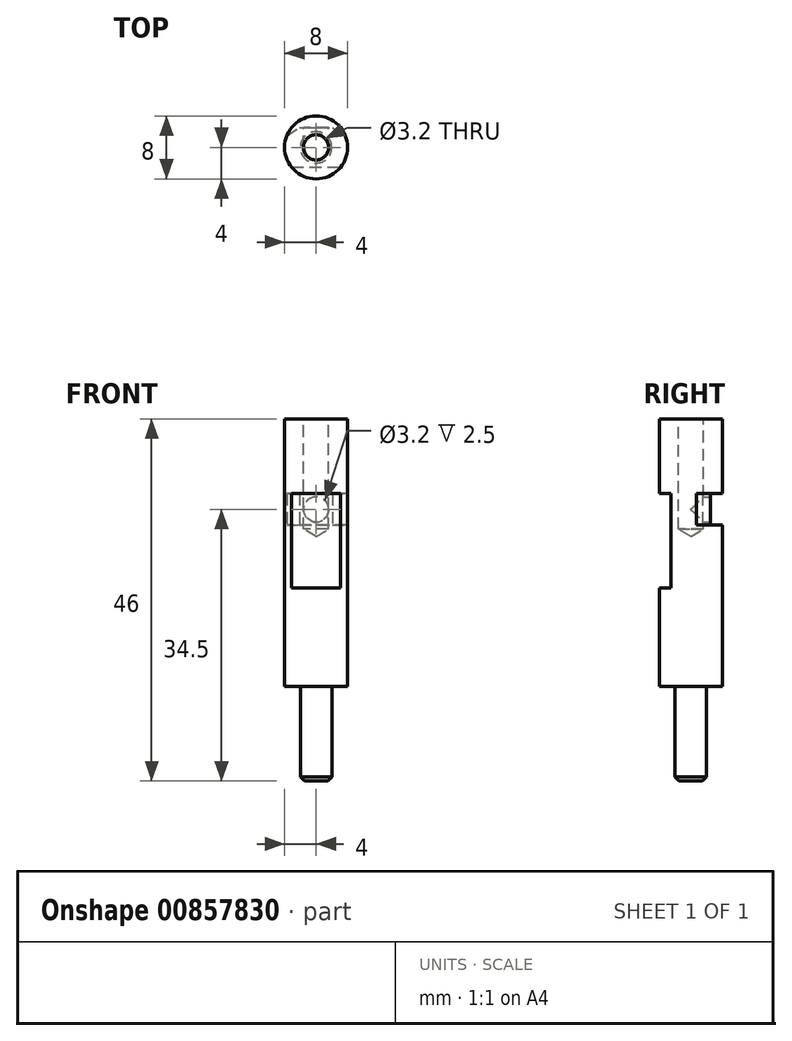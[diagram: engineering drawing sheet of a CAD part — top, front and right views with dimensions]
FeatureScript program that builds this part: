
annotation { "Feature Type Name" : "Feature", "Feature Type Description" : "" }
export const myFeature = defineFeature(function(context is Context, id is Id, definition is map)
    precondition{}
    {
        {
            var Q0;
            Q0=qCreatedBy(makeId("Front.planeOp"),FACE);
            var sketch = newSketch(context, id + "F0", { "sketchPlane" : qUnion([Q0])});
            skLineSegment(sketch, "E0", {"start": v(0, 0) * mm, "end": v(-2, 0) * mm});
            skLineSegment(sketch, "E1", {"start": v(-2, 0) * mm, "end": v(-2, 12) * mm});
            skLineSegment(sketch, "E2", {"start": v(-2, 12) * mm, "end": v(-4, 12) * mm});
            skLineSegment(sketch, "E3", {"start": v(-4, 12) * mm, "end": v(-4, 24.5) * mm});
            skLineSegment(sketch, "E4", {"start": v(-4, 24.5) * mm, "end": v(0, 24.5) * mm});
            skLineSegment(sketch, "E5", {"start": v(0, 24.5) * mm, "end": v(0, 0) * mm});
            skSolve(sketch);
        }
        {
            var Q0;
            Q0=makeQuery(id+"F0.imprint","IMPRINT",FACE,{"disambiguationData":[TD([[makeQuery(id+"F0.imprint","IMPRINT",EDGE,{"derivedFrom":sQuery(id+"F0.wireOp",EDGE,"E0")}),-1.0]])]});
            var Q1;
            Q1=sQuery(id+"F0.wireOp",EDGE,"E5");
            revolve(context, id + "F1", {"surfaceOperationType" : NewSurfaceOperationType.NEW, "entities" : qUnion([Q0]), "axis" : qUnion([Q1]), "revolveType" : RevolveType.FULL});
        }
        {
            var Q0;
            Q0=makeQuery(id+"F1.opRevolve","SWEPT_EDGE",EDGE,{"disambiguationData":[OSD([sQuery(id+"F0.wireOp",EDGE,"E0"),sQuery(id+"F0.wireOp",EDGE,"E1")])]});
            chamfer(context, id + "F2", {"entities" : qUnion([Q0]), "width" : 0.5 * mm, "tangentPropagation" : true});
        }
        {
            var Q0;
            Q0=makeQuery(id+"F1.opRevolve","SWEPT_FACE",FACE,{"disambiguationData":[OSD([sQuery(id+"F0.wireOp",EDGE,"E4")])]});
            var sketch = newSketch(context, id + "F3", { "sketchPlane" : qUnion([Q0])});
            skArc(sketch, "E6.0.0", {"start": v(3.12, -2.5) * mm, "mid": v(0, 4) * mm, "end": v(-3.12, -2.5) * mm});
            skLineSegment(sketch, "E7", {"start": v(-3.12, -2.5) * mm, "end": v(3.12, -2.5) * mm});
            skSolve(sketch);
        }
        {
            var Q0;
            Q0=makeQuery(id+"F3.imprint","IMPRINT",FACE,{"disambiguationData":[TD([[makeQuery(id+"F3.imprint","IMPRINT",EDGE,{"derivedFrom":sQuery(id+"F3.wireOp",EDGE,"E6.0.0")}),1.0]])]});
            extrude(context, id + "F4", {"entities" : qUnion([Q0]), "operationType" : NewBodyOperationType.ADD, "depth" : 8 * mm, "offsetDistance" : 25 * mm});
        }
        {
            var Q0;
            Q0=makeQuery(id+"F4.opExtrude","CAP_FACE",FACE,{"disambiguationData":[OSD([sQuery(id+"F3.wireOp",EDGE,"E6.0.0"),sQuery(id+"F3.wireOp",EDGE,"E7")])],"isStart":false});
            var sketch = newSketch(context, id + "F5", { "sketchPlane" : qUnion([Q0])});
            skArc(sketch, "E8.0.0", {"start": v(3.12, -2.5) * mm, "mid": v(3.88, -0.99) * mm, "end": v(3.94, 0.7) * mm});
            skLineSegment(sketch, "E8.0.1", {"start": v(-3.12, -2.5) * mm, "end": v(3.12, -2.5) * mm});
            skLineSegment(sketch, "E9", {"start": v(-3.7, 1.5) * mm, "end": v(-2.1, 2.5) * mm});
            skLineSegment(sketch, "E10", {"start": v(-2.1, 2.5) * mm, "end": v(2.1, 2.5) * mm});
            skLineSegment(sketch, "E11", {"start": v(2.1, 2.5) * mm, "end": v(3.94, 0.7) * mm});
            skArc(sketch, "E12.trimOffspring", {"start": v(-3.7, 1.5) * mm, "mid": v(-3.96, -0.58) * mm, "end": v(-3.12, -2.5) * mm});
            skSolve(sketch);
        }
        {
            var Q0;
            Q0=makeQuery(id+"F5.imprint","IMPRINT",FACE,{"disambiguationData":[TD([[makeQuery(id+"F5.imprint","IMPRINT",EDGE,{"derivedFrom":sQuery(id+"F5.wireOp",EDGE,"E8.0.0")}),1.0]])]});
            extrude(context, id + "F6", {"entities" : qUnion([Q0]), "operationType" : NewBodyOperationType.ADD, "depth" : 4 * mm, "offsetDistance" : 25 * mm});
        }
        {
            var Q0;
            Q0=makeQuery(id+"F6.opExtrude","CAP_FACE",FACE,{"disambiguationData":[OSD([sQuery(id+"F5.wireOp",EDGE,"E8.0.0"),sQuery(id+"F5.wireOp",EDGE,"E8.0.1"),sQuery(id+"F5.wireOp",EDGE,"E9"),sQuery(id+"F5.wireOp",EDGE,"E10"),sQuery(id+"F5.wireOp",EDGE,"E11"),sQuery(id+"F5.wireOp",EDGE,"E12.trimOffspring")])],"isStart":false});
            var sketch = newSketch(context, id + "F7", { "sketchPlane" : qUnion([Q0])});
            skCircle(sketch, "E13", {"center": v(0, 0) * mm, "radius": 4 * mm});
            skSolve(sketch);
        }
        {
            var Q0;
            Q0 = qSketchRegion(id + "F7", true);
            extrude(context, id + "F8", {"entities" : qUnion([Q0]), "operationType" : NewBodyOperationType.ADD, "depth" : 9.5 * mm, "offsetDistance" : 25 * mm});
        }
        {
            var Q0;
            Q0=makeQuery(id+"F8.opExtrude","CAP_FACE",FACE,{"disambiguationData":[OSD([sQuery(id+"F7.wireOp",EDGE,"E13")])],"isStart":false});
            var sketch = newSketch(context, id + "F9", { "sketchPlane" : qUnion([Q0])});
            skPoint(sketch, "E14", {"position": v(0, 0) * mm});
            skSolve(sketch);
        }
        {
            var Q0;
            Q0=sQuery(id+"F9.wireOp",VERTEX,"E14");
            var Q1;
            Q1=makeQuery(id+"F1.opRevolve","SWEPT_BODY",BODY,{"disambiguationData":[OSD([sQuery(id+"F0.wireOp",EDGE,"E0"),sQuery(id+"F0.wireOp",EDGE,"E1"),sQuery(id+"F0.wireOp",EDGE,"E2"),sQuery(id+"F0.wireOp",EDGE,"E3"),sQuery(id+"F0.wireOp",EDGE,"E4"),sQuery(id+"F0.wireOp",EDGE,"E5")])]});
            hole(context, id + "F10", {"style" : HoleStyle.SIMPLE, "endStyle" : HoleEndStyle.BLIND, "holeDiameter" : 3.2 * mm, "majorDiameter" : 5 * mm, "holeDepth" : 14 * mm, "isTappedThrough" : true, "tappedDepth" : 6 * mm, "tapClearance" : 3, "locations" : qUnion([Q0]), "scope" : qUnion([Q1])});
        }
        {
            var Q0;
            Q0=makeQuery(id+"F6.opExtrude","SWEPT_FACE",FACE,{"disambiguationData":[OSD([sQuery(id+"F5.wireOp",EDGE,"E10")])]});
            var sketch = newSketch(context, id + "F11", { "sketchPlane" : qUnion([Q0])});
            skCircle(sketch, "E15", {"center": v(0, 34.5) * mm, "radius": 1.6 * mm});
            skSolve(sketch);
        }
        {
            var Q0;
            Q0=makeQuery(id+"F11.imprint","IMPRINT",FACE,{"disambiguationData":[TD([[makeQuery(id+"F11.imprint","IMPRINT",EDGE,{"derivedFrom":sQuery(id+"F11.wireOp",EDGE,"E15")}),1.0]])]});
            extrude(context, id + "F12", {"entities" : qUnion([Q0]), "operationType" : NewBodyOperationType.REMOVE, "oppositeDirection" : true, "depth" : 2.53 * mm, "offsetDistance" : 25 * mm});
        }
    });
